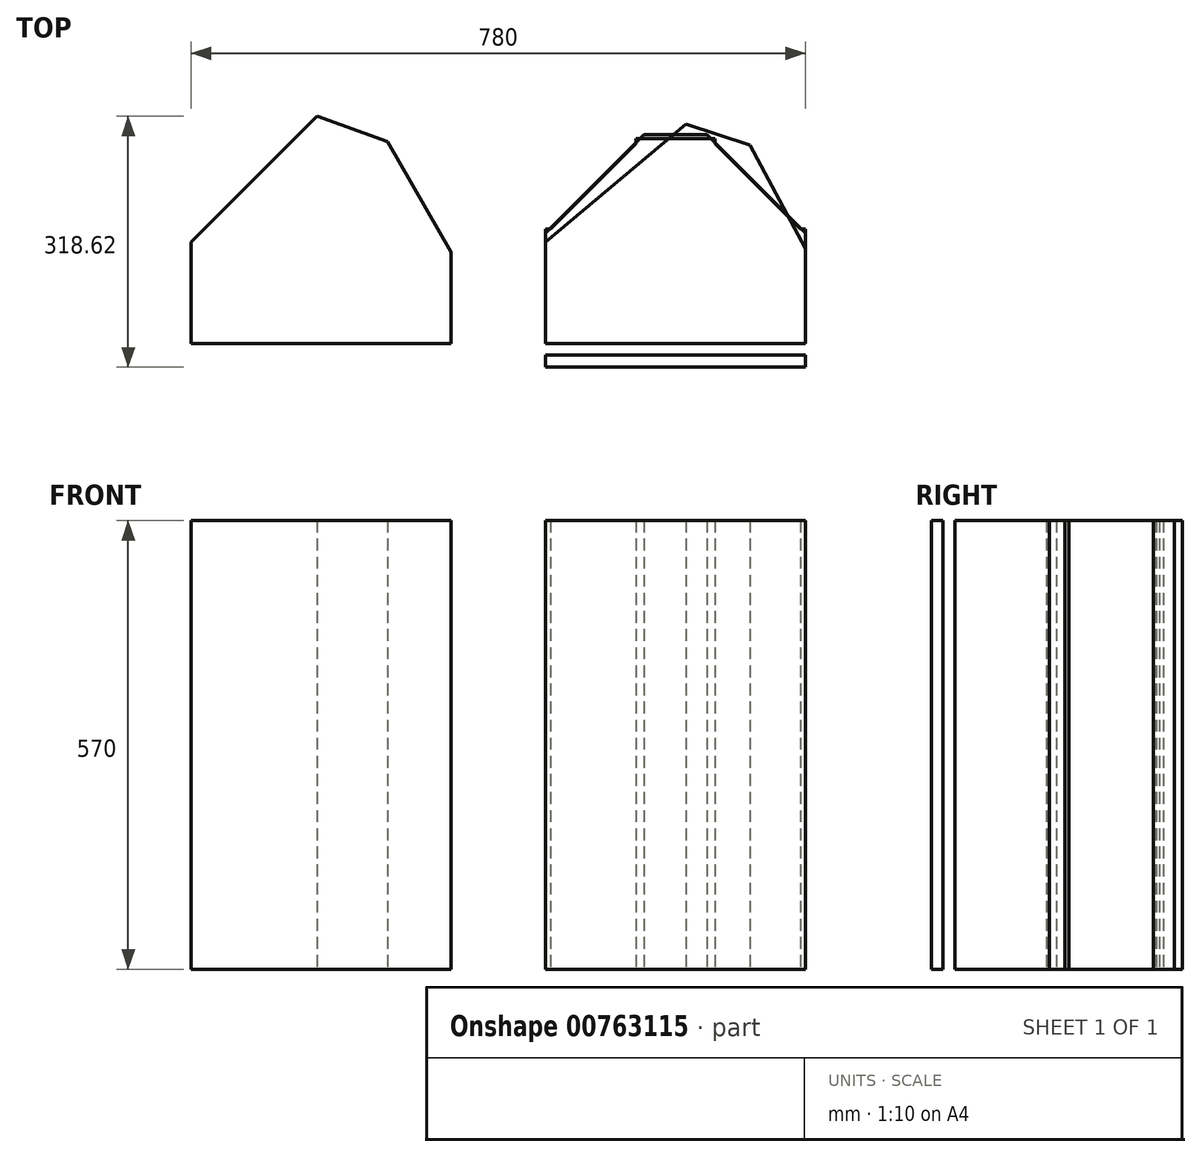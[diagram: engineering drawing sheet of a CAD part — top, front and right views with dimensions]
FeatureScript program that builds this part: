
annotation { "Feature Type Name" : "Feature", "Feature Type Description" : "" }
export const myFeature = defineFeature(function(context is Context, id is Id, definition is map)
    precondition{}
    {
        {
            var Q0;
            Q0=qCreatedBy(makeId("Top.planeOp"),FACE);
            var sketch = newSketch(context, id + "F0", { "sketchPlane" : qUnion([Q0])});
            skLineSegment(sketch, "E0", {"start": v(0, 0) * mm, "end": v(360, 0) * mm});
            skLineSegment(sketch, "E1", {"start": v(360, 0) * mm, "end": v(360, 154) * mm});
            skLineSegment(sketch, "E2", {"start": v(360, 154) * mm, "end": v(284.98, 294.19) * mm});
            skLineSegment(sketch, "E3", {"start": v(284.98, 294.19) * mm, "end": v(189.98, 325.41) * mm});
            skLineSegment(sketch, "E4", {"start": v(189.98, 325.41) * mm, "end": v(0, 166) * mm});
            skLineSegment(sketch, "E5", {"start": v(0, 166) * mm, "end": v(0, 0) * mm});
            skSolve(sketch);
        }
        {
            var Q0;
            Q0=qCreatedBy(makeId("Top.planeOp"),FACE);
            var sketch = newSketch(context, id + "F1", { "sketchPlane" : qUnion([Q0])});
            skLineSegment(sketch, "E6", {"start": v(15, 30) * mm, "end": v(15, 159) * mm});
            skLineSegment(sketch, "E7", {"start": v(15, 159) * mm, "end": v(193.23, 308.55) * mm});
            skLineSegment(sketch, "E8", {"start": v(193.23, 308.55) * mm, "end": v(274.59, 281.81) * mm});
            skLineSegment(sketch, "E9", {"start": v(274.59, 281.81) * mm, "end": v(345, 150.24) * mm});
            skLineSegment(sketch, "E10", {"start": v(345, 150.24) * mm, "end": v(345, 30) * mm});
            skLineSegment(sketch, "E11", {"start": v(345, 30) * mm, "end": v(15, 30) * mm});
            skSolve(sketch);
        }
        {
            var Q0;
            Q0=makeQuery(id+"F1.imprint","IMPRINT",FACE,{"disambiguationData":[TD([[makeQuery(id+"F1.imprint","IMPRINT",EDGE,{"derivedFrom":sQuery(id+"F1.wireOp",EDGE,"E6")}),-1.0]])]});
            extrude(context, id + "F2", {"entities" : qUnion([Q0]), "depth" : 570 * mm, "offsetDistance" : 25 * mm});
        }
        {
            var Q0;
            Q0=qCreatedBy(makeId("Top.planeOp"),FACE);
            var sketch = newSketch(context, id + "F3", { "sketchPlane" : qUnion([Q0])});
            skLineSegment(sketch, "E12.bottom", {"start": v(15, 30) * mm, "end": v(345, 30) * mm});
            skLineSegment(sketch, "E12.left", {"start": v(15, 0) * mm, "end": v(15, 175) * mm});
            skLineSegment(sketch, "E12.right", {"start": v(345, 0) * mm, "end": v(345, 175) * mm});
            skLineSegment(sketch, "E13", {"start": v(21.21, 175) * mm, "end": v(130, 283.79) * mm});
            skLineSegment(sketch, "E14", {"start": v(130, 290) * mm, "end": v(230, 290) * mm});
            skLineSegment(sketch, "E15", {"start": v(230, 283.79) * mm, "end": v(338.79, 175) * mm});
            skLineSegment(sketch, "E16", {"start": v(0, 0) * mm, "end": v(360, 0) * mm});
            skLineSegment(sketch, "E17", {"start": v(360, 0) * mm, "end": v(360, 175) * mm});
            skLineSegment(sketch, "E18", {"start": v(360, 175) * mm, "end": v(230, 305) * mm});
            skLineSegment(sketch, "E19", {"start": v(230, 305) * mm, "end": v(130, 305) * mm});
            skLineSegment(sketch, "E20", {"start": v(130, 305) * mm, "end": v(0, 175) * mm});
            skLineSegment(sketch, "E21", {"start": v(0, 175) * mm, "end": v(0, 0) * mm});
            skLineSegment(sketch, "E22", {"start": v(0, 175) * mm, "end": v(21.21, 175) * mm});
            skLineSegment(sketch, "E23", {"start": v(180, 0) * mm, "end": v(180, 305) * mm, "construction": true});
            skLineSegment(sketch, "E24", {"start": v(130, 305) * mm, "end": v(130, 283.79) * mm});
            skLineSegment(sketch, "E25", {"start": v(230, 305) * mm, "end": v(230, 283.79) * mm});
            skLineSegment(sketch, "E26", {"start": v(15, 15) * mm, "end": v(345, 15) * mm});
            skLineSegment(sketch, "E27", {"start": v(360, 175) * mm, "end": v(338.79, 175) * mm});
            skLineSegment(sketch, "E28", {"start": v(0, 0) * mm, "end": v(0, -20) * mm});
            skLineSegment(sketch, "E29", {"start": v(0, -20) * mm, "end": v(360, -20) * mm});
            skLineSegment(sketch, "E30", {"start": v(360, -20) * mm, "end": v(360, 0) * mm});
            skSolve(sketch);
        }
        {
            var Q0;
            Q0=qCreatedBy(makeId("Top.planeOp"),FACE);
            var sketch = newSketch(context, id + "F4", { "sketchPlane" : qUnion([Q0])});
            skLineSegment(sketch, "E31.bottom", {"start": v(15, 30) * mm, "end": v(345, 30) * mm});
            skLineSegment(sketch, "E31.top", {"start": v(15, 295) * mm, "end": v(345, 295) * mm});
            skLineSegment(sketch, "E31.left", {"start": v(15, 30) * mm, "end": v(15, 295) * mm});
            skLineSegment(sketch, "E31.right", {"start": v(345, 30) * mm, "end": v(345, 295) * mm});
            skLineSegment(sketch, "E32", {"start": v(15, 191.21) * mm, "end": v(118.79, 295) * mm});
            skLineSegment(sketch, "E33", {"start": v(15, 170) * mm, "end": v(140, 295) * mm});
            skLineSegment(sketch, "E34", {"start": v(241.21, 295) * mm, "end": v(345, 191.21) * mm});
            skLineSegment(sketch, "E35", {"start": v(220, 295) * mm, "end": v(345, 170) * mm});
            skLineSegment(sketch, "E36.bottom", {"start": v(0, 0) * mm, "end": v(360, 0) * mm});
            skLineSegment(sketch, "E36.top", {"start": v(0, 310) * mm, "end": v(360, 310) * mm});
            skLineSegment(sketch, "E36.left", {"start": v(0, 0) * mm, "end": v(0, 310) * mm});
            skLineSegment(sketch, "E36.right", {"start": v(360, 0) * mm, "end": v(360, 310) * mm});
            skLineSegment(sketch, "E37", {"start": v(15, 295) * mm, "end": v(15, 310) * mm});
            skLineSegment(sketch, "E38", {"start": v(15, 30) * mm, "end": v(15, 0) * mm});
            skLineSegment(sketch, "E39", {"start": v(345, 295) * mm, "end": v(345, 310) * mm});
            skLineSegment(sketch, "E40", {"start": v(345, 30) * mm, "end": v(345, 0) * mm});
            skLineSegment(sketch, "E41", {"start": v(15, 15) * mm, "end": v(345, 15) * mm});
            skSolve(sketch);
        }
        {
            var Q0;
            {var subQ1=sQuery(id+"F4.wireOp",EDGE,"E31.bottom");Q0=makeQuery(id+"F4.imprint","IMPRINT",FACE,{"disambiguationData":[TD([[makeQuery(id+"F4.imprint","IMPRINT",EDGE,{"derivedFrom":subQ1}),1.0]])]});}
            extrude(context, id + "F5", {"entities" : qUnion([Q0]), "depth" : 570 * mm, "offsetDistance" : 25 * mm});
        }
        {
            var Q0;
            {var subQ5=sQuery(id+"F4.wireOp",EDGE,"E41");Q0=makeQuery(id+"F4.imprint","IMPRINT",FACE,{"disambiguationData":[TD([[makeQuery(id+"F4.imprint","IMPRINT",EDGE,{"derivedFrom":subQ5}),-1.0]])]});}
            extrude(context, id + "F6", {"entities" : qUnion([Q0]), "depth" : 570 * mm, "offsetDistance" : 25 * mm});
        }
        {
            var Q0;
            Q0=qCreatedBy(makeId("Top.planeOp"),FACE);
            var sketch = newSketch(context, id + "F7", { "sketchPlane" : qUnion([Q0])});
            skLineSegment(sketch, "E42", {"start": v(-450, 0) * mm, "end": v(-90, 0) * mm});
            skLineSegment(sketch, "E43", {"start": v(-90, 0) * mm, "end": v(-90, 150) * mm});
            skLineSegment(sketch, "E44", {"start": v(-90, 150) * mm, "end": v(-175.65, 298.36) * mm});
            skLineSegment(sketch, "E45", {"start": v(-175.65, 298.36) * mm, "end": v(-279.02, 335.98) * mm});
            skLineSegment(sketch, "E46", {"start": v(-279.02, 335.98) * mm, "end": v(-450, 165) * mm});
            skLineSegment(sketch, "E47", {"start": v(-450, 165) * mm, "end": v(-450, 0) * mm});
            skLineSegment(sketch, "E48", {"start": v(-435, 30) * mm, "end": v(-435, 158.79) * mm});
            skLineSegment(sketch, "E49", {"start": v(-435, 158.79) * mm, "end": v(-275.17, 318.62) * mm});
            skLineSegment(sketch, "E50", {"start": v(-275.17, 318.62) * mm, "end": v(-185.91, 286.13) * mm});
            skLineSegment(sketch, "E51", {"start": v(-185.91, 286.13) * mm, "end": v(-105, 145.98) * mm});
            skLineSegment(sketch, "E52", {"start": v(-105, 145.98) * mm, "end": v(-105, 30) * mm});
            skLineSegment(sketch, "E53", {"start": v(-105, 30) * mm, "end": v(-435, 30) * mm});
            skLineSegment(sketch, "E54", {"start": v(-90, 150) * mm, "end": v(-107.32, 150) * mm});
            skLineSegment(sketch, "E55", {"start": v(-90, 150) * mm, "end": v(-105, 141.34) * mm});
            skLineSegment(sketch, "E56", {"start": v(-450, 165) * mm, "end": v(-435, 158.79) * mm});
            skLineSegment(sketch, "E57", {"start": v(-450, 165) * mm, "end": v(-435, 150) * mm});
            skSolve(sketch);
        }
        {
            var Q0;
            Q0=makeQuery(id+"F7.imprint","IMPRINT",FACE,{"disambiguationData":[TD([[makeQuery(id+"F7.imprint","IMPRINT",EDGE,{"derivedFrom":sQuery(id+"F7.wireOp",EDGE,"E48")}),-1.0]])]});
            extrude(context, id + "F8", {"entities" : qUnion([Q0]), "depth" : 570 * mm, "offsetDistance" : 25 * mm});
        }
        {
            var Q0;
            {var subQ2=sQuery(id+"F3.wireOp",EDGE,"E12.bottom");Q0=makeQuery(id+"F3.imprint","IMPRINT",FACE,{"disambiguationData":[TD([[makeQuery(id+"F3.imprint","IMPRINT",EDGE,{"derivedFrom":subQ2}),1.0]])]});}
            extrude(context, id + "F9", {"entities" : qUnion([Q0]), "depth" : 570 * mm, "offsetDistance" : 25 * mm});
        }
    });
